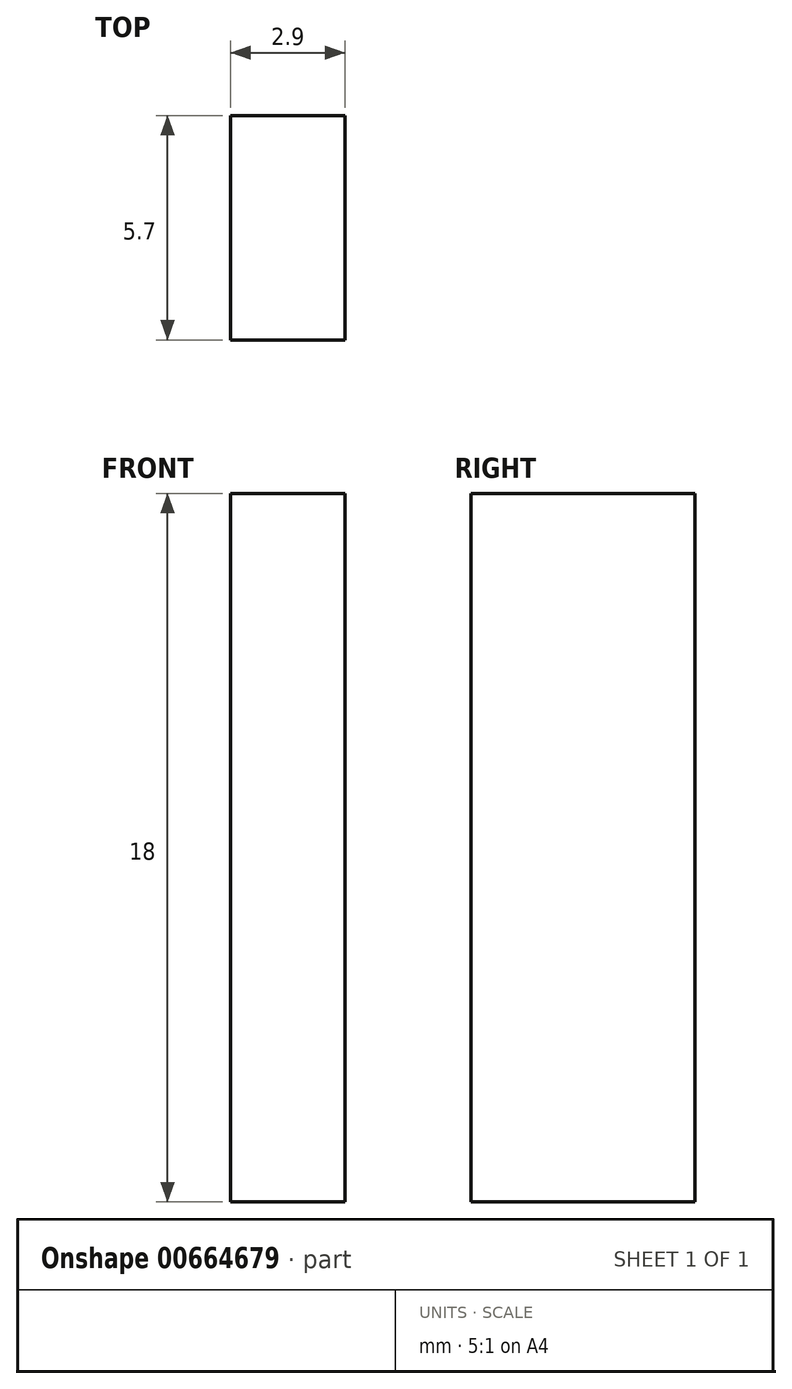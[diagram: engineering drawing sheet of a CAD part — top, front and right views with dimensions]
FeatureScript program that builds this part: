
annotation { "Feature Type Name" : "Feature", "Feature Type Description" : "" }
export const myFeature = defineFeature(function(context is Context, id is Id, definition is map)
    precondition{}
    {
        {
            var Q0;
            Q0=qCreatedBy(makeId("Top.planeOp"),FACE);
            var sketch = newSketch(context, id + "F0", { "sketchPlane" : qUnion([Q0])});
            skLineSegment(sketch, "E0.bottom", {"start": v(0, 0) * mm, "end": v(2.9, 0) * mm});
            skLineSegment(sketch, "E0.top", {"start": v(0, -5.7) * mm, "end": v(2.9, -5.7) * mm});
            skLineSegment(sketch, "E0.left", {"start": v(0, 0) * mm, "end": v(0, -5.7) * mm});
            skLineSegment(sketch, "E0.right", {"start": v(2.9, 0) * mm, "end": v(2.9, -5.7) * mm});
            skSolve(sketch);
        }
        {
            var Q0;
            Q0 = qSketchRegion(id + "F0", true);
            extrude(context, id + "F1", {"entities" : qUnion([Q0]), "depth" : 18 * mm, "offsetDistance" : 25 * mm});
        }
    });
